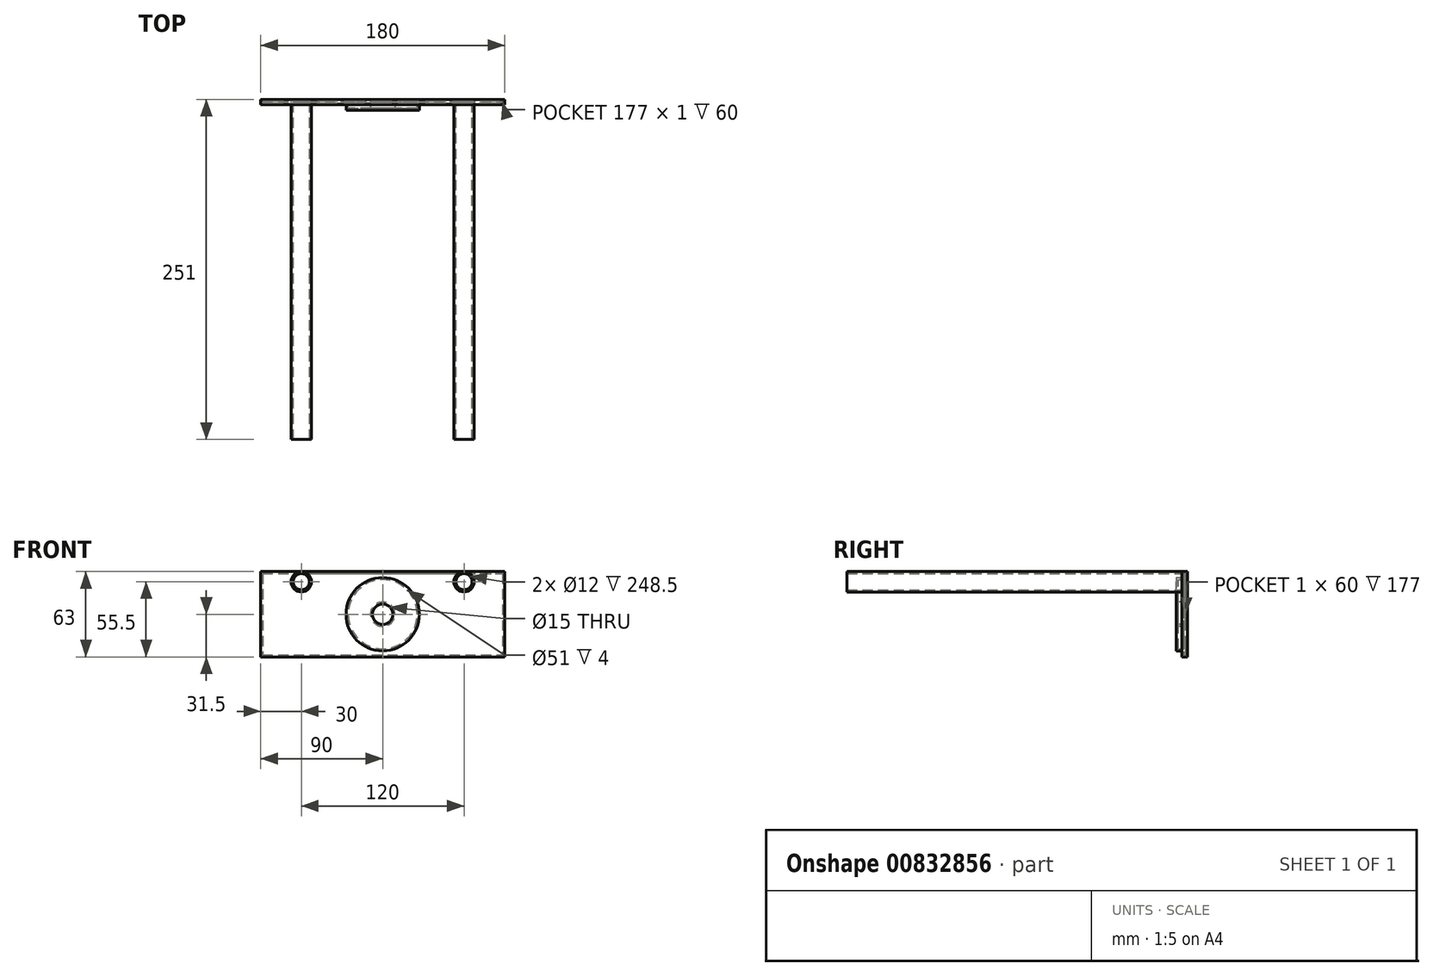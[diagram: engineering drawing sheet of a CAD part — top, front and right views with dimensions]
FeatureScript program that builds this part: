
annotation { "Feature Type Name" : "Feature", "Feature Type Description" : "" }
export const myFeature = defineFeature(function(context is Context, id is Id, definition is map)
    precondition{}
    {
        {
            var Q0;
            Q0=qCreatedBy(makeId("Front.planeOp"),FACE);
            var sketch = newSketch(context, id + "F0", { "sketchPlane" : qUnion([Q0])});
            skLineSegment(sketch, "E0.bottom", {"start": v(0, 0) * mm, "end": v(180, 0) * mm});
            skLineSegment(sketch, "E0.top", {"start": v(0, -63) * mm, "end": v(180, -63) * mm});
            skLineSegment(sketch, "E0.left", {"start": v(0, 0) * mm, "end": v(0, -63) * mm});
            skLineSegment(sketch, "E0.right", {"start": v(180, 0) * mm, "end": v(180, -63) * mm});
            skSolve(sketch);
        }
        {
            var Q0;
            Q0 = qSketchRegion(id + "F0", true);
            extrude(context, id + "F1", {"entities" : qUnion([Q0]), "depth" : 4 * mm, "offsetDistance" : 25 * mm});
        }
        {
            var Q0;
            Q0=makeQuery(id+"F1.opExtrude","CAP_FACE",FACE,{"disambiguationData":[OSD([sQuery(id+"F0.wireOp",EDGE,"E0.bottom"),sQuery(id+"F0.wireOp",EDGE,"E0.top"),sQuery(id+"F0.wireOp",EDGE,"E0.left"),sQuery(id+"F0.wireOp",EDGE,"E0.right")])],"isStart":false});
            var sketch = newSketch(context, id + "F2", { "sketchPlane" : qUnion([Q0])});
            skCircle(sketch, "E1", {"center": v(90, -31.5) * mm, "radius": 27 * mm});
            skCircle(sketch, "E2", {"center": v(150, -7.5) * mm, "radius": 7.5 * mm});
            skCircle(sketch, "E3", {"center": v(30, -7.5) * mm, "radius": 7.5 * mm});
            skLineSegment(sketch, "E4", {"start": v(30, -7.5) * mm, "end": v(0, -7.5) * mm, "construction": true});
            skLineSegment(sketch, "E5", {"start": v(150, -7.5) * mm, "end": v(180, -7.5) * mm, "construction": true});
            skSolve(sketch);
        }
        {
            var Q0;
            Q0=makeQuery(id+"F2.imprint","IMPRINT",FACE,{"disambiguationData":[TD([[makeQuery(id+"F2.imprint","IMPRINT",EDGE,{"derivedFrom":sQuery(id+"F2.wireOp",EDGE,"E1")}),1.0]])]});
            extrude(context, id + "F3", {"entities" : qUnion([Q0]), "operationType" : NewBodyOperationType.ADD, "depth" : 4 * mm, "offsetDistance" : 25 * mm});
        }
        {
            var Q0;
            Q0=makeQuery(id+"F2.imprint","IMPRINT",FACE,{"disambiguationData":[TD([[makeQuery(id+"F2.imprint","IMPRINT",EDGE,{"derivedFrom":sQuery(id+"F2.wireOp",EDGE,"E3")}),1.0]])]});
            var Q1;
            Q1=makeQuery(id+"F2.imprint","IMPRINT",FACE,{"disambiguationData":[TD([[makeQuery(id+"F2.imprint","IMPRINT",EDGE,{"derivedFrom":sQuery(id+"F2.wireOp",EDGE,"E2")}),1.0]])]});
            extrude(context, id + "F4", {"entities" : qUnion([Q0, Q1]), "operationType" : NewBodyOperationType.ADD, "depth" : 247 * mm, "offsetDistance" : 25 * mm});
        }
        {
            var Q0;
            Q0=makeQuery(id+"F3.opExtrude","CAP_FACE",FACE,{"disambiguationData":[OSD([sQuery(id+"F2.wireOp",EDGE,"E1")])],"isStart":false});
            var sketch = newSketch(context, id + "F5", { "sketchPlane" : qUnion([Q0])});
            skCircle(sketch, "E6", {"center": v(90, -31.5) * mm, "radius": 7.5 * mm});
            skSolve(sketch);
        }
        {
            var Q0;
            Q0 = qSketchRegion(id + "F5", true);
            extrude(context, id + "F6", {"entities" : qUnion([Q0]), "operationType" : NewBodyOperationType.REMOVE, "oppositeDirection" : true, "depth" : 25 * mm, "offsetDistance" : 25 * mm});
        }
        {
            var Q0;
            Q0=makeQuery(id+"F4.opExtrude","CAP_FACE",FACE,{"disambiguationData":[OSD([sQuery(id+"F2.wireOp",EDGE,"E3")])],"isStart":false});
            var Q1;
            Q1=makeQuery(id+"F4.opExtrude","CAP_FACE",FACE,{"disambiguationData":[OSD([sQuery(id+"F2.wireOp",EDGE,"E2")])],"isStart":false});
            shell(context, id + "F7", {"entities" : qUnion([Q0, Q1]), "thickness" : 1.5 * mm});
        }
    });
